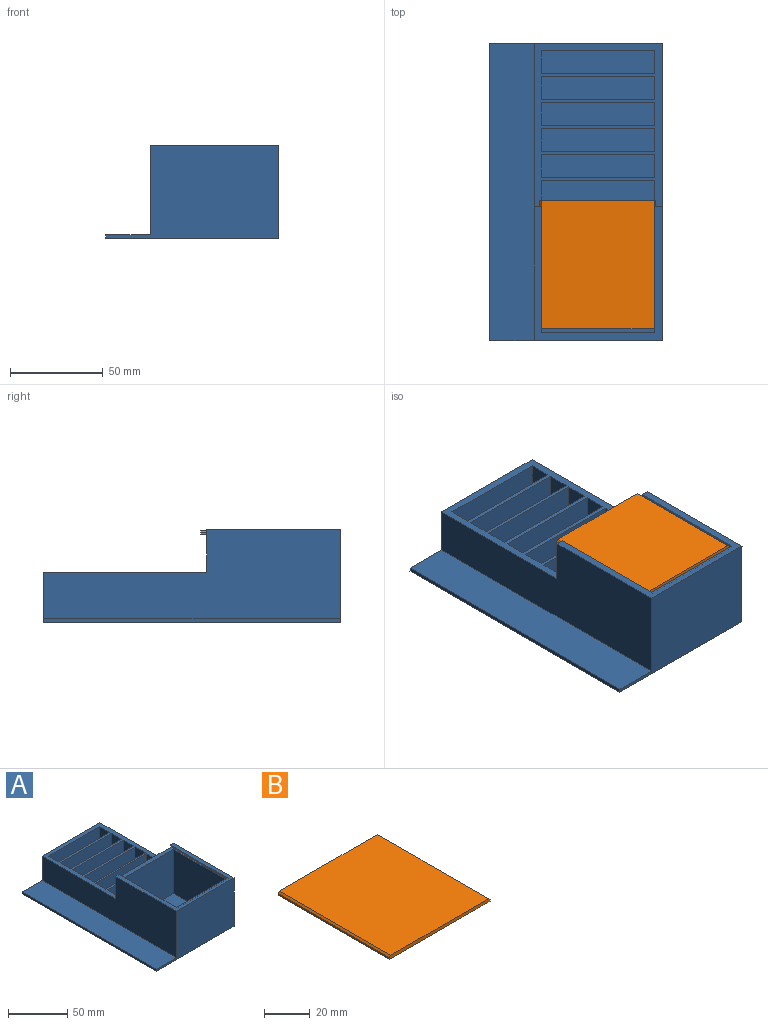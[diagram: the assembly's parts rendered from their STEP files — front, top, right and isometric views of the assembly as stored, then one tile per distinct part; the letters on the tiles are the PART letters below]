
ASSEMBLY  parts=2 mates=1
PART A: 55 faces, bbox 93x160x50 mm
  f0: plane 69x23mm, normal (0,1,0), area 1431.5mm2, adj f1,f2,f4,f5,f9,f12,f44,f45
  f1: plane 72x69mm, normal (0,0,1), area 820mm2, adj f0,f2,f3,f4,f8,f9,f12
  f2: plane 68x0.5mm, normal (1,0,0), area 34mm2, adj f0,f1,f3,f48
  f3: plane 61x0.5mm, normal (0,1,0), area 30.5mm2, adj f1,f2,f4,f43
  f4: plane 68x0.5mm, normal (-1,0,0), area 34mm2, adj f0,f1,f3,f44
  f5: plane 88x69mm, normal (0,0,1), area 1680mm2, adj f0,f6,f9,f12,f13,f14,f15,f16
  f6: plane 93x27mm, normal (0,1,0), area 1911mm2, adj f5,f7,f9,f10,f11,f12
  f7: plane 160x2mm, normal (-1,0,0), area 320mm2, adj f6,f8,f10,f11
  f8: plane 93x50mm, normal (0,-1,0), area 3498mm2, adj f1,f7,f9,f10,f11,f12
  f9: plane 160x50mm, normal (1,0,0), area 5976mm2, adj f0,f1,f5,f6,f8,f11
  f10: plane 160x24mm, normal (0,0,1), area 3840mm2, adj f6,f7,f8,f12
  f11: plane 160x93mm, normal (0,0,-1), area 14880mm2, adj f6,f7,f8,f9
  f12: plane 160x48mm, normal (-1,0,0), area 5656mm2, adj f0,f1,f5,f6,f8,f10
  f13: plane 61x25mm, normal (0,-1,0), area 1525mm2, adj f5,f14,f16,f17
  f14: plane 25x12mm, normal (1,0,0), area 300mm2, adj f5,f13,f15,f17
  f15: plane 61x25mm, normal (0,1,0), area 1525mm2, adj f5,f14,f16,f17
  f16: plane 25x12mm, normal (-1,0,0), area 300mm2, adj f5,f13,f15,f17
  f17: plane 61x12mm, normal (0,0,1), area 732mm2, adj f13,f14,f15,f16
  f18: plane 61x25mm, normal (0,-1,0), area 1525mm2, adj f5,f19,f21,f22
  f19: plane 25x12mm, normal (1,0,0), area 300mm2, adj f5,f18,f20,f22
  f20: plane 61x25mm, normal (0,1,0), area 1525mm2, adj f5,f19,f21,f22
  f21: plane 25x12mm, normal (-1,0,0), area 300mm2, adj f5,f18,f20,f22
  f22: plane 61x12mm, normal (0,0,1), area 732mm2, adj f18,f19,f20,f21
  f23: plane 61x25mm, normal (0,-1,0), area 1525mm2, adj f5,f24,f26,f27
  f24: plane 25x12mm, normal (1,0,0), area 300mm2, adj f5,f23,f25,f27
  f25: plane 61x25mm, normal (0,1,0), area 1525mm2, adj f5,f24,f26,f27
  f26: plane 25x12mm, normal (-1,0,0), area 300mm2, adj f5,f23,f25,f27
  f27: plane 61x12mm, normal (0,0,1), area 732mm2, adj f23,f24,f25,f26
  f28: plane 61x25mm, normal (0,-1,0), area 1525mm2, adj f5,f29,f31,f32
  f29: plane 25x12mm, normal (1,0,0), area 300mm2, adj f5,f28,f30,f32
  f30: plane 61x25mm, normal (0,1,0), area 1525mm2, adj f5,f29,f31,f32
  f31: plane 25x12mm, normal (-1,0,0), area 300mm2, adj f5,f28,f30,f32
  f32: plane 61x12mm, normal (0,0,1), area 732mm2, adj f28,f29,f30,f31
  f33: plane 61x25mm, normal (0,-1,0), area 1525mm2, adj f5,f34,f36,f37
  f34: plane 25x12mm, normal (1,0,0), area 300mm2, adj f5,f33,f35,f37
  f35: plane 61x25mm, normal (0,1,0), area 1525mm2, adj f5,f34,f36,f37
  f36: plane 25x12mm, normal (-1,0,0), area 300mm2, adj f5,f33,f35,f37
  f37: plane 61x12mm, normal (0,0,1), area 732mm2, adj f33,f34,f35,f36
  f38: plane 61x25mm, normal (0,-1,0), area 1525mm2, adj f5,f39,f41,f42
  f39: plane 25x12mm, normal (1,0,0), area 300mm2, adj f5,f38,f40,f42
  f40: plane 61x25mm, normal (0,1,0), area 1525mm2, adj f5,f39,f41,f42
  f41: plane 25x12mm, normal (-1,0,0), area 300mm2, adj f5,f38,f40,f42
  f42: plane 61x12mm, normal (0,0,1), area 732mm2, adj f38,f39,f40,f41
  f43: plane 61x1mm, normal (0,0,-1), area 61mm2, adj f3,f44,f48,f49
  f44: plane 69x1mm, normal (-0.71,0,-0.71), area 97.6mm2, adj f0,f4,f43,f45,f49
  f45: plane 69x1mm, normal (-1,0,0), area 69mm2, adj f0,f44,f46,f49
  f46: plane 69x63mm, normal (0,0,1), area 443mm2, adj f0,f45,f47,f49,f51,f52,f53,f54
  f47: plane 69x1mm, normal (1,0,0), area 69mm2, adj f0,f46,f48,f49
  f48: plane 69x1mm, normal (0.71,0,-0.71), area 97.6mm2, adj f0,f2,f43,f47,f49
  f49: plane 63x2mm, normal (0,1,0), area 125mm2, adj f43,f44,f45,f46,f47,f48
  f50: plane 64x61mm, normal (0,0,1), area 3904mm2, adj f51,f52,f53,f54
  f51: plane 64x45.5mm, normal (-1,0,0), area 2912mm2, adj f46,f50,f52,f54
  f52: plane 61x45.5mm, normal (0,1,0), area 2775.5mm2, adj f46,f50,f51,f53
  f53: plane 64x45.5mm, normal (1,0,0), area 2912mm2, adj f46,f50,f52,f54
  f54: plane 61x45.5mm, normal (0,-1,0), area 2775.5mm2, adj f46,f50,f51,f53
PART B: 8 faces, bbox 62.5x69x1.8 mm
  f0: plane 69x60.7mm, normal (0,0,1), area 4188.3mm2, adj f1,f5,f6,f7
  f1: plane 69x0.9mm, normal (-0.71,0,0.71), area 87.8mm2, adj f0,f2,f6,f7
  f2: plane 69x0.9mm, normal (-1,0,0), area 62.1mm2, adj f1,f3,f6,f7
  f3: plane 69x62.5mm, normal (0,0,-1), area 4312.5mm2, adj f2,f4,f6,f7
  f4: plane 69x0.9mm, normal (1,0,0), area 62.1mm2, adj f3,f5,f6,f7
  f5: plane 69x0.9mm, normal (0.71,0,0.71), area 87.8mm2, adj f0,f4,f6,f7
  f6: plane 62.5x1.8mm, normal (0,-1,0), area 111.7mm2, adj f0,f1,f2,f3,f4,f5
  f7: plane 62.5x1.8mm, normal (0,1,0), area 111.7mm2, adj f0,f1,f2,f3,f4,f5
PLACE A rot(axis=(0.01,0.65,-0.76),0deg) t=(116.39,-112.65,81.51)mm
PLACE B t=(133.43,-116.54,92.2)mm
MATE slider B.f6 <-> A.f0  axis (0,-1,0) through (99.88,-185.54,129.01)mm
